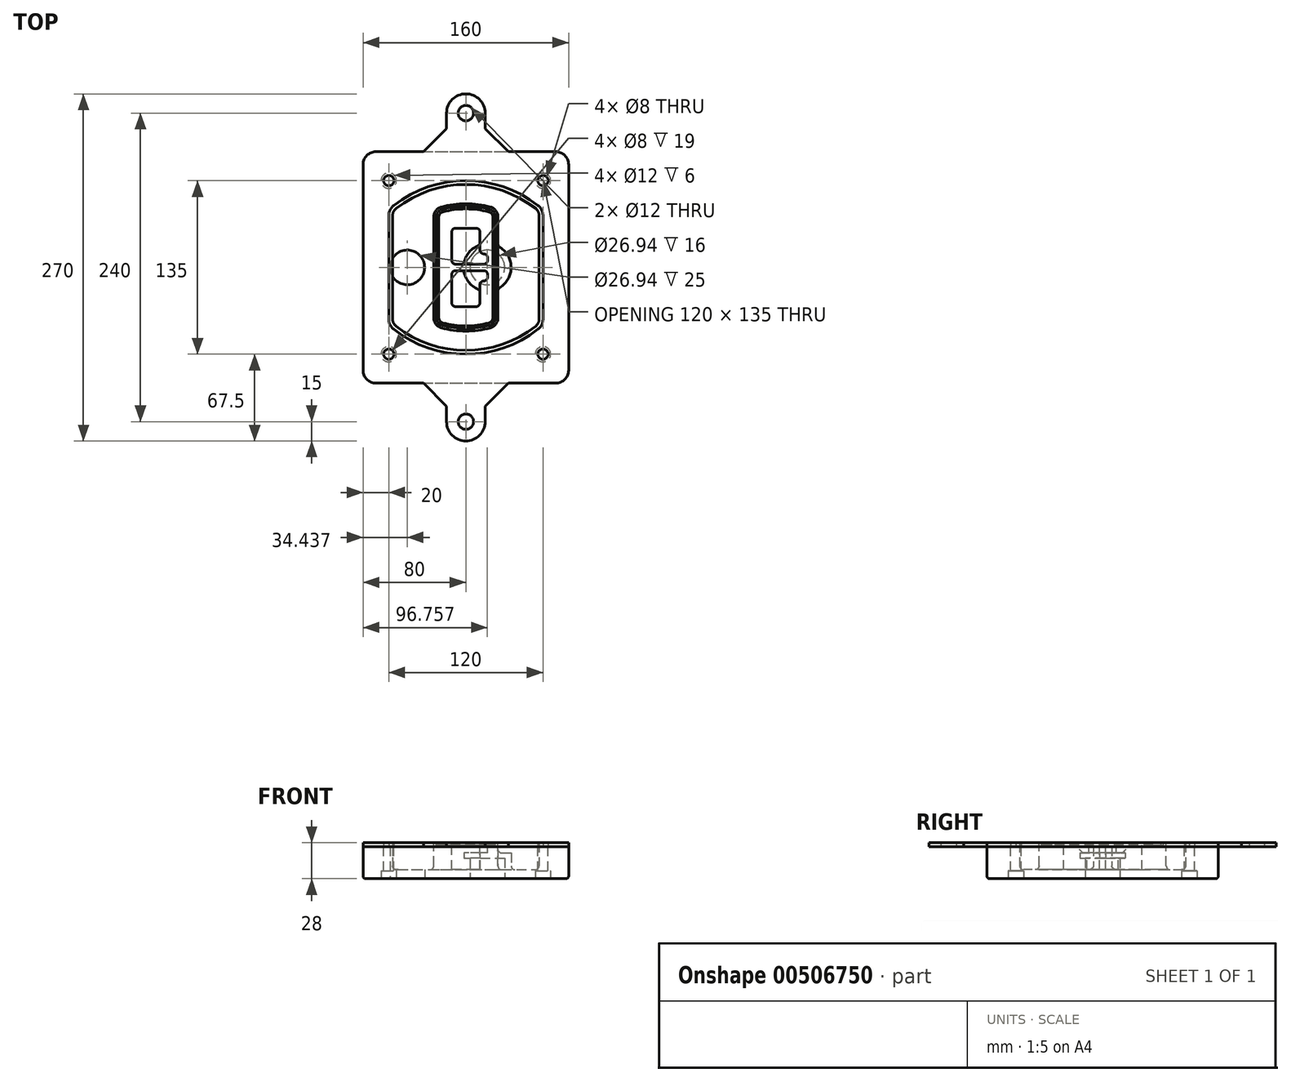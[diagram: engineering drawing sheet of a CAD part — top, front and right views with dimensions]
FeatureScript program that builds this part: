
annotation { "Feature Type Name" : "Feature", "Feature Type Description" : "" }
export const myFeature = defineFeature(function(context is Context, id is Id, definition is map)
    precondition{}
    {
        {
            var Q0;
            Q0=qCreatedBy(makeId("Top.planeOp"),FACE);
            var sketch = newSketch(context, id + "F0", { "sketchPlane" : qUnion([Q0])});
            skPoint(sketch, "E0.rect.middle", {"position": v(0, 0) * mm});
            skLineSegment(sketch, "E1.bottom", {"start": v(-70, -90) * mm, "end": v(70, -90) * mm});
            skLineSegment(sketch, "E1.top", {"start": v(-70, 90) * mm, "end": v(70, 90) * mm});
            skLineSegment(sketch, "E1.left", {"start": v(-80, -80) * mm, "end": v(-80, 80) * mm});
            skLineSegment(sketch, "E1.right", {"start": v(80, -80) * mm, "end": v(80, 80) * mm});
            skLineSegment(sketch, "E2", {"start": v(-80, 90) * mm, "end": v(80, -90) * mm, "construction": true});
            skLineSegment(sketch, "E3", {"start": v(80, 90) * mm, "end": v(-80, -90) * mm, "construction": true});
            skCircle(sketch, "E4", {"center": v(-60, 67.5) * mm, "radius": 4 * mm});
            skCircle(sketch, "E5", {"center": v(60, 67.5) * mm, "radius": 4 * mm});
            skCircle(sketch, "E6", {"center": v(60, -67.5) * mm, "radius": 4 * mm});
            skCircle(sketch, "E7", {"center": v(-60, -67.5) * mm, "radius": 4 * mm});
            skLineSegment(sketch, "E8", {"start": v(-60, 67.5) * mm, "end": v(60, 67.5) * mm, "construction": true});
            skLineSegment(sketch, "E9", {"start": v(60, 67.5) * mm, "end": v(60, -67.5) * mm, "construction": true});
            skLineSegment(sketch, "E10", {"start": v(60, -67.5) * mm, "end": v(-60, -67.5) * mm, "construction": true});
            skLineSegment(sketch, "E11", {"start": v(-60, -67.5) * mm, "end": v(-60, 67.5) * mm, "construction": true});
            skLineSegment(sketch, "E12", {"start": v(-60, 40.3) * mm, "end": v(-60, -40.3) * mm});
            skLineSegment(sketch, "E13", {"start": v(60, 40.3) * mm, "end": v(60, -40.3) * mm});
            skArc(sketch, "E14", {"start": v(56.15, 48.18) * mm, "mid": v(0, 67.5) * mm, "end": v(-56.15, 48.18) * mm});
            skArc(sketch, "E15", {"start": v(-56.15, -48.18) * mm, "mid": v(0, -67.5) * mm, "end": v(56.15, -48.18) * mm});
            skLineSegment(sketch, "E16", {"start": v(-60, 0) * mm, "end": v(60, 0) * mm, "construction": true});
            skPoint(sketch, "E17.visualSharp", {"position": v(-60, -45) * mm});
            skArc(sketch, "E17.filletArc", {"start": v(-60, -40.3) * mm, "mid": v(-58.99, -44.68) * mm, "end": v(-56.15, -48.18) * mm});
            skPoint(sketch, "E18.visualSharp", {"position": v(-60, 45) * mm});
            skArc(sketch, "E18.filletArc", {"start": v(-56.15, 48.18) * mm, "mid": v(-58.99, 44.68) * mm, "end": v(-60, 40.3) * mm});
            skPoint(sketch, "E19.visualSharp", {"position": v(60, 45) * mm});
            skArc(sketch, "E19.filletArc", {"start": v(60, 40.3) * mm, "mid": v(58.99, 44.68) * mm, "end": v(56.15, 48.18) * mm});
            skPoint(sketch, "E20.visualSharp", {"position": v(60, -45) * mm});
            skArc(sketch, "E20.filletArc", {"start": v(56.15, -48.18) * mm, "mid": v(58.99, -44.68) * mm, "end": v(60, -40.3) * mm});
            skPoint(sketch, "E21.visualSharp", {"position": v(-80, 90) * mm});
            skArc(sketch, "E21.filletArc", {"start": v(-70, 90) * mm, "mid": v(-77.07, 87.07) * mm, "end": v(-80, 80) * mm});
            skPoint(sketch, "E22.visualSharp", {"position": v(80, 90) * mm});
            skArc(sketch, "E22.filletArc", {"start": v(80, 80) * mm, "mid": v(77.07, 87.07) * mm, "end": v(70, 90) * mm});
            skPoint(sketch, "E23.visualSharp", {"position": v(80, -90) * mm});
            skArc(sketch, "E23.filletArc", {"start": v(70, -90) * mm, "mid": v(77.07, -87.07) * mm, "end": v(80, -80) * mm});
            skPoint(sketch, "E24.visualSharp", {"position": v(-80, -90) * mm});
            skArc(sketch, "E24.filletArc", {"start": v(-80, -80) * mm, "mid": v(-77.07, -87.07) * mm, "end": v(-70, -90) * mm});
            skArc(sketch, "E25.0", {"start": v(57, 40.3) * mm, "mid": v(56.3, 43.36) * mm, "end": v(54.3, 45.81) * mm});
            skLineSegment(sketch, "E25.1", {"start": v(57, 40.3) * mm, "end": v(57, -40.3) * mm});
            skArc(sketch, "E25.2", {"start": v(54.3, -45.81) * mm, "mid": v(56.3, -43.36) * mm, "end": v(57, -40.3) * mm});
            skArc(sketch, "E25.3", {"start": v(-54.3, -45.81) * mm, "mid": v(0, -64.5) * mm, "end": v(54.3, -45.81) * mm});
            skArc(sketch, "E25.4", {"start": v(-57, -40.3) * mm, "mid": v(-56.3, -43.36) * mm, "end": v(-54.3, -45.81) * mm});
            skArc(sketch, "E25.5", {"start": v(54.3, 45.81) * mm, "mid": v(0, 64.5) * mm, "end": v(-54.3, 45.81) * mm});
            skLineSegment(sketch, "E25.6", {"start": v(-57, 40.3) * mm, "end": v(-57, -40.3) * mm});
            skArc(sketch, "E25.7", {"start": v(-54.3, 45.81) * mm, "mid": v(-56.3, 43.36) * mm, "end": v(-57, 40.3) * mm});
            skArc(sketch, "E26.0", {"start": v(-58.62, 51.33) * mm, "mid": v(-62.58, 46.43) * mm, "end": v(-64, 40.3) * mm});
            skArc(sketch, "E26.1", {"start": v(58.62, 51.33) * mm, "mid": v(0, 71.5) * mm, "end": v(-58.62, 51.33) * mm});
            skArc(sketch, "E26.2", {"start": v(64, 40.3) * mm, "mid": v(62.58, 46.43) * mm, "end": v(58.62, 51.33) * mm});
            skLineSegment(sketch, "E26.3", {"start": v(64, 40.3) * mm, "end": v(64, -40.3) * mm});
            skArc(sketch, "E26.4", {"start": v(58.62, -51.33) * mm, "mid": v(62.58, -46.43) * mm, "end": v(64, -40.3) * mm});
            skLineSegment(sketch, "E26.5", {"start": v(-64, 40.3) * mm, "end": v(-64, -40.3) * mm});
            skArc(sketch, "E26.6", {"start": v(-58.62, -51.33) * mm, "mid": v(0, -71.5) * mm, "end": v(58.62, -51.33) * mm});
            skArc(sketch, "E26.7", {"start": v(-64, -40.3) * mm, "mid": v(-62.58, -46.43) * mm, "end": v(-58.62, -51.33) * mm});
            skSolve(sketch);
        }
        {
            var Q0;
            Q0=makeQuery(id+"F0.imprint","IMPRINT",FACE,{"disambiguationData":[TD([[makeQuery(id+"F0.imprint","IMPRINT",EDGE,{"derivedFrom":sQuery(id+"F0.wireOp",EDGE,"E1.bottom")}),1.0]])]});
            var Q1;
            Q1=makeQuery(id+"F0.imprint","IMPRINT",FACE,{"disambiguationData":[TD([[makeQuery(id+"F0.imprint","IMPRINT",EDGE,{"derivedFrom":sQuery(id+"F0.wireOp",EDGE,"E12")}),1.0]])]});
            var Q2;
            Q2=makeQuery(id+"F0.imprint","IMPRINT",FACE,{"disambiguationData":[TD([[makeQuery(id+"F0.imprint","IMPRINT",EDGE,{"derivedFrom":sQuery(id+"F0.wireOp",EDGE,"E25.0")}),1.0]])]});
            var Q3;
            Q3=makeQuery(id+"F0.imprint","IMPRINT",FACE,{"disambiguationData":[TD([[makeQuery(id+"F0.imprint","IMPRINT",EDGE,{"derivedFrom":sQuery(id+"F0.wireOp",EDGE,"E12")}),-1.0]])]});
            extrude(context, id + "F1", {"entities" : qUnion([Q0, Q1, Q2, Q3]), "oppositeDirection" : true, "depth" : 25 * mm});
        }
        {
            var Q0;
            Q0=makeQuery(id+"F0.imprint","IMPRINT",FACE,{"disambiguationData":[TD([[makeQuery(id+"F0.imprint","IMPRINT",EDGE,{"derivedFrom":sQuery(id+"F0.wireOp",EDGE,"E12")}),1.0]])]});
            extrude(context, id + "F2", {"entities" : qUnion([Q0]), "operationType" : NewBodyOperationType.ADD, "depth" : 3 * mm});
        }
        {
            var Q0;
            Q0=makeQuery(id+"F0.imprint","IMPRINT",FACE,{"disambiguationData":[TD([[makeQuery(id+"F0.imprint","IMPRINT",EDGE,{"derivedFrom":sQuery(id+"F0.wireOp",EDGE,"E25.0")}),1.0]])]});
            extrude(context, id + "F3", {"entities" : qUnion([Q0]), "operationType" : NewBodyOperationType.REMOVE, "oppositeDirection" : true, "depth" : 18 * mm});
        }
        {
            var Q0;
            Q0=makeQuery(id+"F2.opExtrude","CAP_FACE",FACE,{"disambiguationData":[OSD([sQuery(id+"F0.wireOp",EDGE,"E12"),sQuery(id+"F0.wireOp",EDGE,"E13"),sQuery(id+"F0.wireOp",EDGE,"E14"),sQuery(id+"F0.wireOp",EDGE,"E15"),sQuery(id+"F0.wireOp",EDGE,"E17.filletArc"),sQuery(id+"F0.wireOp",EDGE,"E18.filletArc"),sQuery(id+"F0.wireOp",EDGE,"E19.filletArc"),sQuery(id+"F0.wireOp",EDGE,"E20.filletArc"),sQuery(id+"F0.wireOp",EDGE,"E25.0"),sQuery(id+"F0.wireOp",EDGE,"E25.1"),sQuery(id+"F0.wireOp",EDGE,"E25.2"),sQuery(id+"F0.wireOp",EDGE,"E25.3"),sQuery(id+"F0.wireOp",EDGE,"E25.4"),sQuery(id+"F0.wireOp",EDGE,"E25.5"),sQuery(id+"F0.wireOp",EDGE,"E25.6"),sQuery(id+"F0.wireOp",EDGE,"E25.7")])],"isStart":false});
            var sketch = newSketch(context, id + "F4", { "sketchPlane" : qUnion([Q0])});
            skArc(sketch, "E27.0", {"start": v(-19.08, -46.97) * mm, "mid": v(0, -49.5) * mm, "end": v(19.08, -46.97) * mm});
            skArc(sketch, "E28.0", {"start": v(19.08, 46.97) * mm, "mid": v(0, 49.5) * mm, "end": v(-19.08, 46.97) * mm});
            skLineSegment(sketch, "E29", {"start": v(-25, 39.25) * mm, "end": v(-25, -39.25) * mm});
            skLineSegment(sketch, "E30", {"start": v(25, 39.25) * mm, "end": v(25, -39.25) * mm});
            skLineSegment(sketch, "E31", {"start": v(-25, 45.1) * mm, "end": v(25, 45.1) * mm, "construction": true});
            skLineSegment(sketch, "E32", {"start": v(-25, -45.1) * mm, "end": v(25, -45.1) * mm, "construction": true});
            skPoint(sketch, "E33.visualSharp", {"position": v(-25, 45.1) * mm});
            skArc(sketch, "E33.filletArc", {"start": v(-19.08, 46.97) * mm, "mid": v(-23.35, 44.11) * mm, "end": v(-25, 39.25) * mm});
            skPoint(sketch, "E34.visualSharp", {"position": v(25, 45.1) * mm});
            skArc(sketch, "E34.filletArc", {"start": v(25, 39.25) * mm, "mid": v(23.35, 44.11) * mm, "end": v(19.08, 46.97) * mm});
            skPoint(sketch, "E35.visualSharp", {"position": v(25, -45.1) * mm});
            skArc(sketch, "E35.filletArc", {"start": v(19.08, -46.97) * mm, "mid": v(23.35, -44.11) * mm, "end": v(25, -39.25) * mm});
            skPoint(sketch, "E36.visualSharp", {"position": v(-25, -45.1) * mm});
            skArc(sketch, "E36.filletArc", {"start": v(-25, -39.25) * mm, "mid": v(-23.35, -44.11) * mm, "end": v(-19.08, -46.97) * mm});
            skArc(sketch, "E37.0", {"start": v(54.3, 45.81) * mm, "mid": v(0, 64.5) * mm, "end": v(-54.3, 45.81) * mm});
            skArc(sketch, "E37.1", {"start": v(-54.3, 45.81) * mm, "mid": v(-56.3, 43.36) * mm, "end": v(-57, 40.3) * mm});
            skLineSegment(sketch, "E37.2", {"start": v(-57, 40.3) * mm, "end": v(-57, -40.3) * mm});
            skArc(sketch, "E37.3", {"start": v(-57, -40.3) * mm, "mid": v(-56.3, -43.36) * mm, "end": v(-54.3, -45.81) * mm});
            skArc(sketch, "E37.4", {"start": v(-54.3, -45.81) * mm, "mid": v(0, -64.5) * mm, "end": v(54.3, -45.81) * mm});
            skArc(sketch, "E37.5", {"start": v(54.3, -45.81) * mm, "mid": v(56.3, -43.36) * mm, "end": v(57, -40.3) * mm});
            skLineSegment(sketch, "E37.6", {"start": v(57, 40.3) * mm, "end": v(57, -40.3) * mm});
            skArc(sketch, "E37.7", {"start": v(57, 40.3) * mm, "mid": v(56.3, 43.36) * mm, "end": v(54.3, 45.81) * mm});
            skLineSegment(sketch, "E38.0", {"start": v(23, 39.25) * mm, "end": v(23, -39.25) * mm});
            skArc(sketch, "E38.1", {"start": v(18.56, -45.04) * mm, "mid": v(21.76, -42.9) * mm, "end": v(23, -39.25) * mm});
            skArc(sketch, "E38.2", {"start": v(-18.56, -45.04) * mm, "mid": v(0, -47.5) * mm, "end": v(18.56, -45.04) * mm});
            skArc(sketch, "E38.3", {"start": v(-23, -39.25) * mm, "mid": v(-21.76, -42.9) * mm, "end": v(-18.56, -45.04) * mm});
            skLineSegment(sketch, "E38.4", {"start": v(-23, 39.25) * mm, "end": v(-23, -39.25) * mm});
            skArc(sketch, "E38.5", {"start": v(23, 39.25) * mm, "mid": v(21.76, 42.9) * mm, "end": v(18.56, 45.04) * mm});
            skArc(sketch, "E38.6", {"start": v(-18.56, 45.04) * mm, "mid": v(-21.76, 42.9) * mm, "end": v(-23, 39.25) * mm});
            skArc(sketch, "E38.7", {"start": v(18.56, 45.04) * mm, "mid": v(0, 47.5) * mm, "end": v(-18.56, 45.04) * mm});
            skArc(sketch, "E39.0", {"start": v(21, 39.25) * mm, "mid": v(20.18, 41.68) * mm, "end": v(18.04, 43.1) * mm});
            skLineSegment(sketch, "E39.1", {"start": v(21, 39.25) * mm, "end": v(21, -39.25) * mm});
            skArc(sketch, "E39.2", {"start": v(18.04, -43.1) * mm, "mid": v(20.18, -41.68) * mm, "end": v(21, -39.25) * mm});
            skArc(sketch, "E39.3", {"start": v(-18.04, -43.1) * mm, "mid": v(0, -45.5) * mm, "end": v(18.04, -43.1) * mm});
            skArc(sketch, "E39.4", {"start": v(-21, -39.25) * mm, "mid": v(-20.18, -41.68) * mm, "end": v(-18.04, -43.1) * mm});
            skArc(sketch, "E39.5", {"start": v(18.04, 43.1) * mm, "mid": v(0, 45.5) * mm, "end": v(-18.04, 43.1) * mm});
            skLineSegment(sketch, "E39.6", {"start": v(-21, 39.25) * mm, "end": v(-21, -39.25) * mm});
            skArc(sketch, "E39.7", {"start": v(-18.04, 43.1) * mm, "mid": v(-20.18, 41.68) * mm, "end": v(-21, 39.25) * mm});
            skLineSegment(sketch, "E40", {"start": v(-25, 0) * mm, "end": v(25, 0) * mm, "construction": true});
            skLineSegment(sketch, "E41", {"start": v(-11, 5.5) * mm, "end": v(-11, 27.5) * mm});
            skLineSegment(sketch, "E42", {"start": v(-8, 30.5) * mm, "end": v(8, 30.5) * mm});
            skLineSegment(sketch, "E43", {"start": v(11, 27.5) * mm, "end": v(11, 13.5) * mm});
            skLineSegment(sketch, "E44", {"start": v(14, 10.5) * mm, "end": v(14, 10.5) * mm});
            skLineSegment(sketch, "E45", {"start": v(17, 7.5) * mm, "end": v(17, 5.5) * mm});
            skLineSegment(sketch, "E46", {"start": v(14, 2.5) * mm, "end": v(-8, 2.5) * mm});
            skPoint(sketch, "E47.visualSharp", {"position": v(-11, 30.5) * mm});
            skArc(sketch, "E47.filletArc", {"start": v(-8, 30.5) * mm, "mid": v(-10.12, 29.62) * mm, "end": v(-11, 27.5) * mm});
            skPoint(sketch, "E48.visualSharp", {"position": v(11, 30.5) * mm});
            skArc(sketch, "E48.filletArc", {"start": v(11, 27.5) * mm, "mid": v(10.12, 29.62) * mm, "end": v(8, 30.5) * mm});
            skPoint(sketch, "E49.visualSharp", {"position": v(11, 10.5) * mm});
            skArc(sketch, "E49.filletArc", {"start": v(11, 13.5) * mm, "mid": v(11.88, 11.38) * mm, "end": v(14, 10.5) * mm});
            skPoint(sketch, "E50.visualSharp", {"position": v(17, 10.5) * mm});
            skArc(sketch, "E50.filletArc", {"start": v(17, 7.5) * mm, "mid": v(16.12, 9.62) * mm, "end": v(14, 10.5) * mm});
            skPoint(sketch, "E51.visualSharp", {"position": v(17, 2.5) * mm});
            skArc(sketch, "E51.filletArc", {"start": v(14, 2.5) * mm, "mid": v(16.12, 3.38) * mm, "end": v(17, 5.5) * mm});
            skPoint(sketch, "E52.visualSharp", {"position": v(-11, 2.5) * mm});
            skArc(sketch, "E52.filletArc", {"start": v(-11, 5.5) * mm, "mid": v(-10.12, 3.38) * mm, "end": v(-8, 2.5) * mm});
            skLineSegment(sketch, "E53.0.MirrorCS", {"start": v(14, -2.5) * mm, "end": v(-8, -2.5) * mm});
            skArc(sketch, "E54.0.MirrorCS", {"start": v(-11, -5.5) * mm, "mid": v(-10.12, -3.38) * mm, "end": v(-8, -2.5) * mm});
            skLineSegment(sketch, "E55.0.MirrorCS", {"start": v(-11, -5.5) * mm, "end": v(-11, -27.5) * mm});
            skArc(sketch, "E56.0.MirrorCS", {"start": v(-8, -30.5) * mm, "mid": v(-10.12, -29.62) * mm, "end": v(-11, -27.5) * mm});
            skLineSegment(sketch, "E57.0.MirrorCS", {"start": v(-8, -30.5) * mm, "end": v(8, -30.5) * mm});
            skArc(sketch, "E58.0.MirrorCS", {"start": v(11, -27.5) * mm, "mid": v(10.12, -29.62) * mm, "end": v(8, -30.5) * mm});
            skLineSegment(sketch, "E59.0.MirrorCS", {"start": v(11, -27.5) * mm, "end": v(11, -13.5) * mm});
            skArc(sketch, "E60.0.MirrorCS", {"start": v(11, -13.5) * mm, "mid": v(11.88, -11.38) * mm, "end": v(14, -10.5) * mm});
            skArc(sketch, "E61.0.MirrorCS", {"start": v(17, -7.5) * mm, "mid": v(16.12, -9.62) * mm, "end": v(14, -10.5) * mm});
            skLineSegment(sketch, "E62.0.MirrorCS", {"start": v(17, -7.5) * mm, "end": v(17, -5.5) * mm});
            skArc(sketch, "E63.0.MirrorCS", {"start": v(14, -2.5) * mm, "mid": v(16.12, -3.38) * mm, "end": v(17, -5.5) * mm});
            skSolve(sketch);
        }
        {
            var Q0;
            Q0=makeQuery(id+"F4.imprint","IMPRINT",FACE,{"disambiguationData":[TD([[makeQuery(id+"F4.imprint","IMPRINT",EDGE,{"derivedFrom":sQuery(id+"F4.wireOp",EDGE,"E27.0")}),1.0]])]});
            var Q1;
            Q1=makeQuery(id+"F4.imprint","IMPRINT",FACE,{"disambiguationData":[TD([[makeQuery(id+"F4.imprint","IMPRINT",EDGE,{"derivedFrom":sQuery(id+"F4.wireOp",EDGE,"E38.0")}),-1.0]])]});
            var Q2;
            Q2=makeQuery(id+"F4.imprint","IMPRINT",FACE,{"disambiguationData":[TD([[makeQuery(id+"F4.imprint","IMPRINT",EDGE,{"derivedFrom":sQuery(id+"F4.wireOp",EDGE,"E39.0")}),1.0]])]});
            extrude(context, id + "F5", {"entities" : qUnion([Q0, Q1, Q2]), "operationType" : NewBodyOperationType.ADD, "endBound" : BoundingType.UP_TO_NEXT, "oppositeDirection" : true, "depth" : 25 * mm});
        }
        {
            var Q0;
            Q0=makeQuery(id+"F4.imprint","IMPRINT",FACE,{"disambiguationData":[TD([[makeQuery(id+"F4.imprint","IMPRINT",EDGE,{"derivedFrom":sQuery(id+"F4.wireOp",EDGE,"E38.0")}),-1.0]])]});
            extrude(context, id + "F6", {"entities" : qUnion([Q0]), "operationType" : NewBodyOperationType.REMOVE, "oppositeDirection" : true, "depth" : 2 * mm});
        }
        {
            var Q0;
            Q0=makeQuery(id+"F1.opExtrude","CAP_FACE",FACE,{"disambiguationData":[OSD([sQuery(id+"F0.wireOp",EDGE,"E1.bottom"),sQuery(id+"F0.wireOp",EDGE,"E1.top"),sQuery(id+"F0.wireOp",EDGE,"E1.left"),sQuery(id+"F0.wireOp",EDGE,"E1.right"),sQuery(id+"F0.wireOp",EDGE,"E4"),sQuery(id+"F0.wireOp",EDGE,"E5"),sQuery(id+"F0.wireOp",EDGE,"E6"),sQuery(id+"F0.wireOp",EDGE,"E7"),sQuery(id+"F0.wireOp",EDGE,"E21.filletArc"),sQuery(id+"F0.wireOp",EDGE,"E22.filletArc"),sQuery(id+"F0.wireOp",EDGE,"E23.filletArc"),sQuery(id+"F0.wireOp",EDGE,"E24.filletArc")])],"isStart":false});
            var sketch = newSketch(context, id + "F7", { "sketchPlane" : qUnion([Q0])});
            skCircle(sketch, "E64", {"center": v(16.76, 0) * mm, "radius": 13.47 * mm});
            skCircle(sketch, "E65", {"center": v(-45.56, 0) * mm, "radius": 13.47 * mm});
            skLineSegment(sketch, "E66", {"start": v(80, 0) * mm, "end": v(-80, 0) * mm});
            skCircle(sketch, "E67", {"center": v(16.76, 0) * mm, "radius": 18.47 * mm});
            skCircle(sketch, "E68", {"center": v(60, -67.5) * mm, "radius": 6 * mm});
            skCircle(sketch, "E69", {"center": v(-60, -67.5) * mm, "radius": 6 * mm});
            skCircle(sketch, "E70", {"center": v(-60, 67.5) * mm, "radius": 6 * mm});
            skCircle(sketch, "E71", {"center": v(60, 67.5) * mm, "radius": 6 * mm});
            skSolve(sketch);
        }
        {
            var Q0;
            {var subQ1=sQuery(id+"F7.wireOp",EDGE,"E66");var subQ4=sQuery(id+"F7.wireOp",EDGE,"E64");var subQ6=makeQuery(id+"F7.imprint","INTERSECT",VERTEX,{"disambiguationData":[OD(0.0)],"derivedFrom":[subQ4,subQ1]});Q0=makeQuery(id+"F7.imprint","IMPRINT",FACE,{"disambiguationData":[TD([[makeQuery(id+"F7.imprint","IMPRINT",EDGE,{"disambiguationData":[TD([[subQ6,-1.0]])],"derivedFrom":subQ4}),-1.0]])]});}
            var Q1;
            {var subQ0=sQuery(id+"F7.wireOp",EDGE,"E66");var subQ1=sQuery(id+"F7.wireOp",EDGE,"E64");var subQ3=makeQuery(id+"F7.imprint","INTERSECT",VERTEX,{"disambiguationData":[OD(0.0)],"derivedFrom":[subQ1,subQ0]});Q1=makeQuery(id+"F7.imprint","IMPRINT",FACE,{"disambiguationData":[TD([[makeQuery(id+"F7.imprint","IMPRINT",EDGE,{"disambiguationData":[TD([[subQ3,-1.0]])],"derivedFrom":subQ1}),1.0]])]});}
            var Q2;
            {var subQ0=sQuery(id+"F7.wireOp",EDGE,"E66");var subQ1=sQuery(id+"F7.wireOp",EDGE,"E64");var subQ3=makeQuery(id+"F7.imprint","INTERSECT",VERTEX,{"disambiguationData":[OD(0.0)],"derivedFrom":[subQ1,subQ0]});Q2=makeQuery(id+"F7.imprint","IMPRINT",FACE,{"disambiguationData":[TD([[makeQuery(id+"F7.imprint","IMPRINT",EDGE,{"disambiguationData":[TD([[subQ3,1.0]])],"derivedFrom":subQ1}),1.0]])]});}
            var Q3;
            {var subQ1=sQuery(id+"F7.wireOp",EDGE,"E66");var subQ4=sQuery(id+"F7.wireOp",EDGE,"E64");var subQ6=makeQuery(id+"F7.imprint","INTERSECT",VERTEX,{"disambiguationData":[OD(0.0)],"derivedFrom":[subQ4,subQ1]});Q3=makeQuery(id+"F7.imprint","IMPRINT",FACE,{"disambiguationData":[TD([[makeQuery(id+"F7.imprint","IMPRINT",EDGE,{"disambiguationData":[TD([[subQ6,1.0]])],"derivedFrom":subQ4}),-1.0]])]});}
            extrude(context, id + "F8", {"entities" : qUnion([Q0, Q1, Q2, Q3]), "operationType" : NewBodyOperationType.ADD, "oppositeDirection" : true, "depth" : 20 * mm});
        }
        {
            var Q0;
            {var subQ0=sQuery(id+"F7.wireOp",EDGE,"E66");var subQ1=sQuery(id+"F7.wireOp",EDGE,"E64");var subQ3=makeQuery(id+"F7.imprint","INTERSECT",VERTEX,{"disambiguationData":[OD(0.0)],"derivedFrom":[subQ1,subQ0]});Q0=makeQuery(id+"F7.imprint","IMPRINT",FACE,{"disambiguationData":[TD([[makeQuery(id+"F7.imprint","IMPRINT",EDGE,{"disambiguationData":[TD([[subQ3,-1.0]])],"derivedFrom":subQ1}),1.0]])]});}
            var Q1;
            {var subQ0=sQuery(id+"F7.wireOp",EDGE,"E66");var subQ1=sQuery(id+"F7.wireOp",EDGE,"E64");var subQ3=makeQuery(id+"F7.imprint","INTERSECT",VERTEX,{"disambiguationData":[OD(0.0)],"derivedFrom":[subQ1,subQ0]});Q1=makeQuery(id+"F7.imprint","IMPRINT",FACE,{"disambiguationData":[TD([[makeQuery(id+"F7.imprint","IMPRINT",EDGE,{"disambiguationData":[TD([[subQ3,1.0]])],"derivedFrom":subQ1}),1.0]])]});}
            extrude(context, id + "F9", {"entities" : qUnion([Q0, Q1]), "operationType" : NewBodyOperationType.REMOVE, "oppositeDirection" : true, "depth" : 16 * mm});
        }
        {
            var Q0;
            {var subQ0=sQuery(id+"F7.wireOp",EDGE,"E66");var subQ1=sQuery(id+"F7.wireOp",EDGE,"E65");var subQ3=makeQuery(id+"F7.imprint","INTERSECT",VERTEX,{"disambiguationData":[OD(0.0)],"derivedFrom":[subQ1,subQ0]});Q0=makeQuery(id+"F7.imprint","IMPRINT",FACE,{"disambiguationData":[TD([[makeQuery(id+"F7.imprint","IMPRINT",EDGE,{"disambiguationData":[TD([[subQ3,-1.0]])],"derivedFrom":subQ1}),1.0]])]});}
            var Q1;
            {var subQ0=sQuery(id+"F7.wireOp",EDGE,"E66");var subQ1=sQuery(id+"F7.wireOp",EDGE,"E65");var subQ3=makeQuery(id+"F7.imprint","INTERSECT",VERTEX,{"disambiguationData":[OD(0.0)],"derivedFrom":[subQ1,subQ0]});Q1=makeQuery(id+"F7.imprint","IMPRINT",FACE,{"disambiguationData":[TD([[makeQuery(id+"F7.imprint","IMPRINT",EDGE,{"disambiguationData":[TD([[subQ3,1.0]])],"derivedFrom":subQ1}),1.0]])]});}
            extrude(context, id + "F10", {"entities" : qUnion([Q0, Q1]), "operationType" : NewBodyOperationType.REMOVE, "oppositeDirection" : true, "depth" : 25 * mm});
        }
        {
            var Q0;
            Q0=makeQuery(id+"F7.imprint","IMPRINT",FACE,{"disambiguationData":[TD([[makeQuery(id+"F7.imprint","IMPRINT",EDGE,{"derivedFrom":sQuery(id+"F7.wireOp",EDGE,"E68")}),1.0]])]});
            var Q1;
            Q1=makeQuery(id+"F7.imprint","IMPRINT",FACE,{"disambiguationData":[TD([[makeQuery(id+"F7.imprint","IMPRINT",EDGE,{"derivedFrom":makeQuery(id+"F1.opExtrude","CAP_EDGE",EDGE,{"disambiguationData":[OSD([sQuery(id+"F0.wireOp",EDGE,"E5")])],"isStart":false})}),-1.0]])]});
            var Q2;
            Q2=makeQuery(id+"F7.imprint","IMPRINT",FACE,{"disambiguationData":[TD([[makeQuery(id+"F7.imprint","IMPRINT",EDGE,{"derivedFrom":sQuery(id+"F7.wireOp",EDGE,"E69")}),1.0]])]});
            var Q3;
            Q3=makeQuery(id+"F7.imprint","IMPRINT",FACE,{"disambiguationData":[TD([[makeQuery(id+"F7.imprint","IMPRINT",EDGE,{"derivedFrom":makeQuery(id+"F1.opExtrude","CAP_EDGE",EDGE,{"disambiguationData":[OSD([sQuery(id+"F0.wireOp",EDGE,"E4")])],"isStart":false})}),-1.0]])]});
            var Q4;
            Q4=makeQuery(id+"F7.imprint","IMPRINT",FACE,{"disambiguationData":[TD([[makeQuery(id+"F7.imprint","IMPRINT",EDGE,{"derivedFrom":sQuery(id+"F7.wireOp",EDGE,"E70")}),1.0]])]});
            var Q5;
            Q5=makeQuery(id+"F7.imprint","IMPRINT",FACE,{"disambiguationData":[TD([[makeQuery(id+"F7.imprint","IMPRINT",EDGE,{"derivedFrom":makeQuery(id+"F1.opExtrude","CAP_EDGE",EDGE,{"disambiguationData":[OSD([sQuery(id+"F0.wireOp",EDGE,"E7")])],"isStart":false})}),-1.0]])]});
            var Q6;
            Q6=makeQuery(id+"F7.imprint","IMPRINT",FACE,{"disambiguationData":[TD([[makeQuery(id+"F7.imprint","IMPRINT",EDGE,{"derivedFrom":sQuery(id+"F7.wireOp",EDGE,"E71")}),1.0]])]});
            var Q7;
            Q7=makeQuery(id+"F7.imprint","IMPRINT",FACE,{"disambiguationData":[TD([[makeQuery(id+"F7.imprint","IMPRINT",EDGE,{"derivedFrom":makeQuery(id+"F1.opExtrude","CAP_EDGE",EDGE,{"disambiguationData":[OSD([sQuery(id+"F0.wireOp",EDGE,"E6")])],"isStart":false})}),-1.0]])]});
            extrude(context, id + "F11", {"entities" : qUnion([Q0, Q1, Q2, Q3, Q4, Q5, Q6, Q7]), "operationType" : NewBodyOperationType.REMOVE, "oppositeDirection" : true, "depth" : 6 * mm});
        }
        {
            var Q0;
            Q0=makeQuery(id+"F9.boolean.opBoolean","COPY",FACE,{"derivedFrom":makeQuery(id+"F9.opExtrude","CAP_FACE",FACE,{"disambiguationData":[OSD([sQuery(id+"F7.wireOp",EDGE,"E64")])],"isStart":false})});
            var sketch = newSketch(context, id + "F12", { "sketchPlane" : qUnion([Q0])});
            skArc(sketch, "E72.0", {"start": v(11, 17.55) * mm, "mid": v(2.57, 11.82) * mm, "end": v(-1.54, 2.5) * mm});
            skArc(sketch, "E72.1", {"start": v(-1.54, -2.5) * mm, "mid": v(2.57, -11.82) * mm, "end": v(11, -17.55) * mm});
            skLineSegment(sketch, "E73", {"start": v(-1.54, -2.5) * mm, "end": v(14, -2.5) * mm});
            skLineSegment(sketch, "E74.0", {"start": v(14, 2.5) * mm, "end": v(-1.54, 2.5) * mm});
            skArc(sketch, "E74.1", {"start": v(14, 2.5) * mm, "mid": v(16.12, 3.38) * mm, "end": v(17, 5.5) * mm});
            skLineSegment(sketch, "E74.2", {"start": v(17, 7.5) * mm, "end": v(17, 5.5) * mm});
            skArc(sketch, "E74.3", {"start": v(17, 7.5) * mm, "mid": v(16.12, 9.62) * mm, "end": v(14, 10.5) * mm});
            skArc(sketch, "E74.4", {"start": v(11, 13.5) * mm, "mid": v(11.88, 11.38) * mm, "end": v(14, 10.5) * mm});
            skLineSegment(sketch, "E74.5", {"start": v(11, 17.55) * mm, "end": v(11, 13.5) * mm});
            skLineSegment(sketch, "E74.7", {"start": v(14, -2.5) * mm, "end": v(-1.54, -2.5) * mm});
            skArc(sketch, "E74.8", {"start": v(14, -2.5) * mm, "mid": v(16.12, -3.38) * mm, "end": v(17, -5.5) * mm});
            skLineSegment(sketch, "E74.9", {"start": v(17, -7.5) * mm, "end": v(17, -5.5) * mm});
            skArc(sketch, "E74.10", {"start": v(17, -7.5) * mm, "mid": v(16.12, -9.62) * mm, "end": v(14, -10.5) * mm});
            skArc(sketch, "E74.11", {"start": v(11, -13.5) * mm, "mid": v(11.88, -11.38) * mm, "end": v(14, -10.5) * mm});
            skLineSegment(sketch, "E74.12", {"start": v(11, -17.55) * mm, "end": v(11, -13.5) * mm});
            skPoint(sketch, "E75.orphan", {"position": v(11, -27.5) * mm});
            skPoint(sketch, "E76.orphan", {"position": v(-8, -2.5) * mm});
            skPoint(sketch, "E77.orphan", {"position": v(-8, 2.5) * mm});
            skPoint(sketch, "E78.orphan", {"position": v(11, 27.5) * mm});
            skSolve(sketch);
        }
        {
            var Q0;
            {var subQ7=sQuery(id+"F12.wireOp",EDGE,"E72.0");var subQ14=sQuery(id+"F12.wireOp",EDGE,"E72.1");var subQ16=sQuery(id+"F12.wireOp",EDGE,"E74.1");var subQ18=sQuery(id+"F12.wireOp",EDGE,"E74.8");Q0=qUnion([makeQuery(id+"F12.imprint","IMPRINT",FACE,{"disambiguationData":[TD([[makeQuery(id+"F12.imprint","IMPRINT",EDGE,{"derivedFrom":subQ7}),1.0]])]}),makeQuery(id+"F12.imprint","IMPRINT",FACE,{"disambiguationData":[TD([[makeQuery(id+"F12.imprint","IMPRINT",EDGE,{"derivedFrom":subQ14}),1.0]])]}),makeQuery(id+"F12.imprint","IMPRINT",FACE,{"disambiguationData":[TD([[makeQuery(id+"F12.imprint","IMPRINT",EDGE,{"derivedFrom":subQ16}),1.0]])]}),makeQuery(id+"F12.imprint","IMPRINT",FACE,{"disambiguationData":[TD([[makeQuery(id+"F12.imprint","IMPRINT",EDGE,{"derivedFrom":subQ18}),-1.0]])]})]);}
            var Q1;
            Q1=makeQuery(id+"F5.boolean.opBoolean","SPLIT",FACE,{"disambiguationData":[TD([makeQuery(id+"F5.opExtrude","SWEPT_FACE",FACE,{"disambiguationData":[OSD([sQuery(id+"F4.wireOp",EDGE,"E41")])]})])],"derivedFrom":makeQuery(id+"F3.boolean.opBoolean","COPY",FACE,{"derivedFrom":makeQuery(id+"F3.opExtrude","CAP_FACE",FACE,{"disambiguationData":[OSD([sQuery(id+"F0.wireOp",EDGE,"E25.0"),sQuery(id+"F0.wireOp",EDGE,"E25.1"),sQuery(id+"F0.wireOp",EDGE,"E25.2"),sQuery(id+"F0.wireOp",EDGE,"E25.3"),sQuery(id+"F0.wireOp",EDGE,"E25.4"),sQuery(id+"F0.wireOp",EDGE,"E25.5"),sQuery(id+"F0.wireOp",EDGE,"E25.6"),sQuery(id+"F0.wireOp",EDGE,"E25.7")])],"isStart":false})})});
            extrude(context, id + "F13", {"entities" : qUnion([Q0]), "operationType" : NewBodyOperationType.REMOVE, "endBound" : BoundingType.UP_TO_SURFACE, "endBoundEntityFace" : qUnion([Q1]), "depth" : 25 * mm});
        }
        {
            var Q0;
            Q0=makeQuery(id+"F3.boolean.opBoolean","COPY",EDGE,{"derivedFrom":makeQuery(id+"F3.opExtrude","CAP_EDGE",EDGE,{"disambiguationData":[OSD([sQuery(id+"F0.wireOp",EDGE,"E25.6")])],"isStart":false})});
            var Q1;
            Q1=makeQuery(id+"F8.boolean.opBoolean","INTERSECT",EDGE,{"derivedFrom":[makeQuery(id+"F5.opExtrude","SWEPT_FACE",FACE,{"disambiguationData":[OSD([sQuery(id+"F4.wireOp",EDGE,"E30")])]}),makeQuery(id+"F8.opExtrude","CAP_FACE",FACE,{"disambiguationData":[OSD([sQuery(id+"F7.wireOp",EDGE,"E67")])],"isStart":false})]});
            var Q2;
            Q2=makeQuery(id+"F8.boolean.opBoolean","INTERSECT",EDGE,{"disambiguationData":[OD(1.0)],"derivedFrom":[makeQuery(id+"F5.opExtrude","SWEPT_FACE",FACE,{"disambiguationData":[OSD([sQuery(id+"F4.wireOp",EDGE,"E30")])]}),makeQuery(id+"F8.opExtrude","SWEPT_FACE",FACE,{"disambiguationData":[OSD([sQuery(id+"F7.wireOp",EDGE,"E67")])]})]});
            var Q3;
            {var subQ0=sQuery(id+"F4.wireOp",EDGE,"E30");Q3=makeQuery(id+"F8.boolean.opBoolean","SPLIT",EDGE,{"disambiguationData":[TD([makeQuery(id+"F5.opExtrude","SWEPT_FACE",FACE,{"disambiguationData":[OSD([sQuery(id+"F4.wireOp",EDGE,"E35.filletArc")])]})])],"derivedFrom":makeQuery(id+"F5.opExtrude","CAP_EDGE",EDGE,{"disambiguationData":[OSD([subQ0])],"isStart":false})});}
            var Q4;
            {var subQ0=sQuery(id+"F0.wireOp",EDGE,"E25.7");var subQ1=sQuery(id+"F0.wireOp",EDGE,"E25.1");var subQ2=sQuery(id+"F0.wireOp",EDGE,"E25.6");var subQ3=sQuery(id+"F0.wireOp",EDGE,"E25.5");var subQ4=sQuery(id+"F0.wireOp",EDGE,"E25.4");var subQ5=sQuery(id+"F0.wireOp",EDGE,"E25.0");var subQ6=sQuery(id+"F0.wireOp",EDGE,"E25.2");var subQ7=sQuery(id+"F0.wireOp",EDGE,"E25.3");Q4=makeQuery(id+"F8.boolean.opBoolean","INTERSECT",EDGE,{"derivedFrom":[makeQuery(id+"F5.boolean.opBoolean","SPLIT",FACE,{"disambiguationData":[TD([makeQuery(id+"F2.opExtrude","SWEPT_FACE",FACE,{"disambiguationData":[OSD([subQ5])]})])],"derivedFrom":makeQuery(id+"F3.boolean.opBoolean","COPY",FACE,{"derivedFrom":makeQuery(id+"F3.opExtrude","CAP_FACE",FACE,{"disambiguationData":[OSD([subQ5,subQ1,subQ6,subQ7,subQ4,subQ3,subQ2,subQ0])],"isStart":false})})}),makeQuery(id+"F8.opExtrude","SWEPT_FACE",FACE,{"disambiguationData":[OSD([sQuery(id+"F7.wireOp",EDGE,"E67")])]})]});}
            var Q5;
            Q5=makeQuery(id+"F8.boolean.opBoolean","INTERSECT",EDGE,{"disambiguationData":[OD(0.0)],"derivedFrom":[makeQuery(id+"F5.opExtrude","SWEPT_FACE",FACE,{"disambiguationData":[OSD([sQuery(id+"F4.wireOp",EDGE,"E30")])]}),makeQuery(id+"F8.opExtrude","SWEPT_FACE",FACE,{"disambiguationData":[OSD([sQuery(id+"F7.wireOp",EDGE,"E67")])]})]});
            fillet(context, id + "F14", {"entities" : qUnion([Q0, Q1, Q2, Q3, Q4, Q5]), "radius" : 3 * mm, "tangentPropagation" : true, "allowEdgeOverflow" : false});
        }
        {
            var Q0;
            Q0=makeQuery(id+"F1.opExtrude","CAP_EDGE",EDGE,{"disambiguationData":[OSD([sQuery(id+"F0.wireOp",EDGE,"E1.bottom")])],"isStart":false});
            fillet(context, id + "F15", {"entities" : qUnion([Q0]), "radius" : 2 * mm, "tangentPropagation" : true, "allowEdgeOverflow" : false});
        }
        {
            var Q0;
            {var subQ0=sQuery(id+"F0.wireOp",EDGE,"E21.filletArc");var subQ1=sQuery(id+"F0.wireOp",EDGE,"E7");var subQ2=sQuery(id+"F0.wireOp",EDGE,"E6");var subQ3=sQuery(id+"F0.wireOp",EDGE,"E5");var subQ4=sQuery(id+"F0.wireOp",EDGE,"E4");var subQ5=sQuery(id+"F0.wireOp",EDGE,"E22.filletArc");var subQ6=sQuery(id+"F0.wireOp",EDGE,"E1.bottom");var subQ7=sQuery(id+"F0.wireOp",EDGE,"E1.right");var subQ8=sQuery(id+"F0.wireOp",EDGE,"E1.top");var subQ9=sQuery(id+"F0.wireOp",EDGE,"E1.left");var subQ10=sQuery(id+"F0.wireOp",EDGE,"E23.filletArc");var subQ11=sQuery(id+"F0.wireOp",EDGE,"E24.filletArc");Q0=makeQuery(id+"F2.boolean.opBoolean","SPLIT",FACE,{"disambiguationData":[TD([makeQuery(id+"F1.opExtrude","SWEPT_FACE",FACE,{"disambiguationData":[OSD([subQ6])]})])],"derivedFrom":makeQuery(id+"F1.opExtrude","CAP_FACE",FACE,{"disambiguationData":[OSD([subQ6,subQ8,subQ9,subQ7,subQ4,subQ3,subQ2,subQ1,subQ0,subQ5,subQ10,subQ11])],"isStart":true})});}
            var sketch = newSketch(context, id + "F16", { "sketchPlane" : qUnion([Q0])});
            skLineSegment(sketch, "E79.0", {"start": v(-80, -80) * mm, "end": v(-80, 80) * mm});
            skLineSegment(sketch, "E79.1", {"start": v(80, -80) * mm, "end": v(80, 80) * mm});
            skLineSegment(sketch, "E79.2", {"start": v(-70, 90) * mm, "end": v(70, 90) * mm});
            skLineSegment(sketch, "E79.3", {"start": v(-70, -90) * mm, "end": v(70, -90) * mm});
            skArc(sketch, "E79.4", {"start": v(-70, 90) * mm, "mid": v(-77.07, 87.07) * mm, "end": v(-80, 80) * mm});
            skCircle(sketch, "E79.5", {"center": v(-60, 67.5) * mm, "radius": 4 * mm});
            skCircle(sketch, "E79.6", {"center": v(60, 67.5) * mm, "radius": 4 * mm});
            skArc(sketch, "E79.7", {"start": v(80, 80) * mm, "mid": v(77.07, 87.07) * mm, "end": v(70, 90) * mm});
            skArc(sketch, "E79.8", {"start": v(70, -90) * mm, "mid": v(77.07, -87.07) * mm, "end": v(80, -80) * mm});
            skLineSegment(sketch, "E79.9", {"start": v(-60, 40.3) * mm, "end": v(-60, -40.3) * mm});
            skArc(sketch, "E79.10", {"start": v(-80, -80) * mm, "mid": v(-77.07, -87.07) * mm, "end": v(-70, -90) * mm});
            skCircle(sketch, "E79.11", {"center": v(-60, -67.5) * mm, "radius": 4 * mm});
            skArc(sketch, "E79.12", {"start": v(-56.15, -48.18) * mm, "mid": v(0, -67.5) * mm, "end": v(56.15, -48.18) * mm});
            skArc(sketch, "E79.13", {"start": v(-60, -40.3) * mm, "mid": v(-58.99, -44.68) * mm, "end": v(-56.15, -48.18) * mm});
            skArc(sketch, "E79.14", {"start": v(56.15, -48.18) * mm, "mid": v(58.99, -44.68) * mm, "end": v(60, -40.3) * mm});
            skCircle(sketch, "E79.15", {"center": v(60, -67.5) * mm, "radius": 4 * mm});
            skLineSegment(sketch, "E79.16", {"start": v(60, 40.3) * mm, "end": v(60, -40.3) * mm});
            skArc(sketch, "E79.17", {"start": v(56.15, 48.18) * mm, "mid": v(0, 67.5) * mm, "end": v(-56.15, 48.18) * mm});
            skArc(sketch, "E79.18", {"start": v(-56.15, 48.18) * mm, "mid": v(-58.99, 44.68) * mm, "end": v(-60, 40.3) * mm});
            skArc(sketch, "E79.19", {"start": v(60, 40.3) * mm, "mid": v(58.99, 44.68) * mm, "end": v(56.15, 48.18) * mm});
            skLineSegment(sketch, "E80", {"start": v(-33, 90) * mm, "end": v(-15, 108) * mm});
            skLineSegment(sketch, "E81", {"start": v(-15, 108) * mm, "end": v(-15, 120) * mm});
            skLineSegment(sketch, "E82", {"start": v(33, 90) * mm, "end": v(15, 108) * mm});
            skLineSegment(sketch, "E83", {"start": v(15, 108) * mm, "end": v(15, 120) * mm});
            skArc(sketch, "E84", {"start": v(15, 120) * mm, "mid": v(0, 135) * mm, "end": v(-15, 120) * mm});
            skLineSegment(sketch, "E85", {"start": v(0, 120) * mm, "end": v(0, 90) * mm, "construction": true});
            skCircle(sketch, "E86", {"center": v(0, 120) * mm, "radius": 6 * mm});
            skLineSegment(sketch, "E87", {"start": v(-80, 0) * mm, "end": v(80, 0) * mm, "construction": true});
            skLineSegment(sketch, "E88.MirrorCS", {"start": v(33, -90) * mm, "end": v(15, -108) * mm});
            skLineSegment(sketch, "E89.MirrorCS", {"start": v(0, -120) * mm, "end": v(0, -90) * mm, "construction": true});
            skLineSegment(sketch, "E90.MirrorCS", {"start": v(-33, -90) * mm, "end": v(-15, -108) * mm});
            skLineSegment(sketch, "E91.MirrorCS", {"start": v(-15, -108) * mm, "end": v(-15, -120) * mm});
            skArc(sketch, "E92.MirrorCS", {"start": v(15, -120) * mm, "mid": v(0, -135) * mm, "end": v(-15, -120) * mm});
            skCircle(sketch, "E93.MirrorC", {"center": v(0, -120) * mm, "radius": 6 * mm});
            skLineSegment(sketch, "E94.MirrorCS", {"start": v(15, -108) * mm, "end": v(15, -120) * mm});
            skArc(sketch, "E95.MirrorCS", {"start": v(80, -80) * mm, "mid": v(77.07, -87.07) * mm, "end": v(70, -90) * mm});
            skSolve(sketch);
        }
        {
            var Q0;
            Q0=makeQuery(id+"F16.imprint","IMPRINT",FACE,{"disambiguationData":[TD([[makeQuery(id+"F16.imprint","IMPRINT",EDGE,{"derivedFrom":sQuery(id+"F16.wireOp",EDGE,"E79.0")}),-1.0]])]});
            var Q1;
            {var subQ1=sQuery(id+"F16.wireOp",EDGE,"E80");Q1=makeQuery(id+"F16.imprint","IMPRINT",FACE,{"disambiguationData":[TD([[makeQuery(id+"F16.imprint","IMPRINT",EDGE,{"derivedFrom":subQ1}),-1.0]])]});}
            var Q2;
            {var subQ1=sQuery(id+"F16.wireOp",EDGE,"E88.MirrorCS");Q2=makeQuery(id+"F16.imprint","IMPRINT",FACE,{"disambiguationData":[TD([[makeQuery(id+"F16.imprint","IMPRINT",EDGE,{"derivedFrom":subQ1}),-1.0]])]});}
            var Q3;
            Q3=makeQuery(id+"F2.opExtrude","CAP_FACE",FACE,{"disambiguationData":[OSD([sQuery(id+"F0.wireOp",EDGE,"E12"),sQuery(id+"F0.wireOp",EDGE,"E13"),sQuery(id+"F0.wireOp",EDGE,"E14"),sQuery(id+"F0.wireOp",EDGE,"E15"),sQuery(id+"F0.wireOp",EDGE,"E17.filletArc"),sQuery(id+"F0.wireOp",EDGE,"E18.filletArc"),sQuery(id+"F0.wireOp",EDGE,"E19.filletArc"),sQuery(id+"F0.wireOp",EDGE,"E20.filletArc"),sQuery(id+"F0.wireOp",EDGE,"E25.0"),sQuery(id+"F0.wireOp",EDGE,"E25.1"),sQuery(id+"F0.wireOp",EDGE,"E25.2"),sQuery(id+"F0.wireOp",EDGE,"E25.3"),sQuery(id+"F0.wireOp",EDGE,"E25.4"),sQuery(id+"F0.wireOp",EDGE,"E25.5"),sQuery(id+"F0.wireOp",EDGE,"E25.6"),sQuery(id+"F0.wireOp",EDGE,"E25.7")])],"isStart":false});
            extrude(context, id + "F17", {"entities" : qUnion([Q0, Q1, Q2]), "endBound" : BoundingType.UP_TO_SURFACE, "endBoundEntityFace" : qUnion([Q3]), "depth" : 4 * mm});
        }
    });
